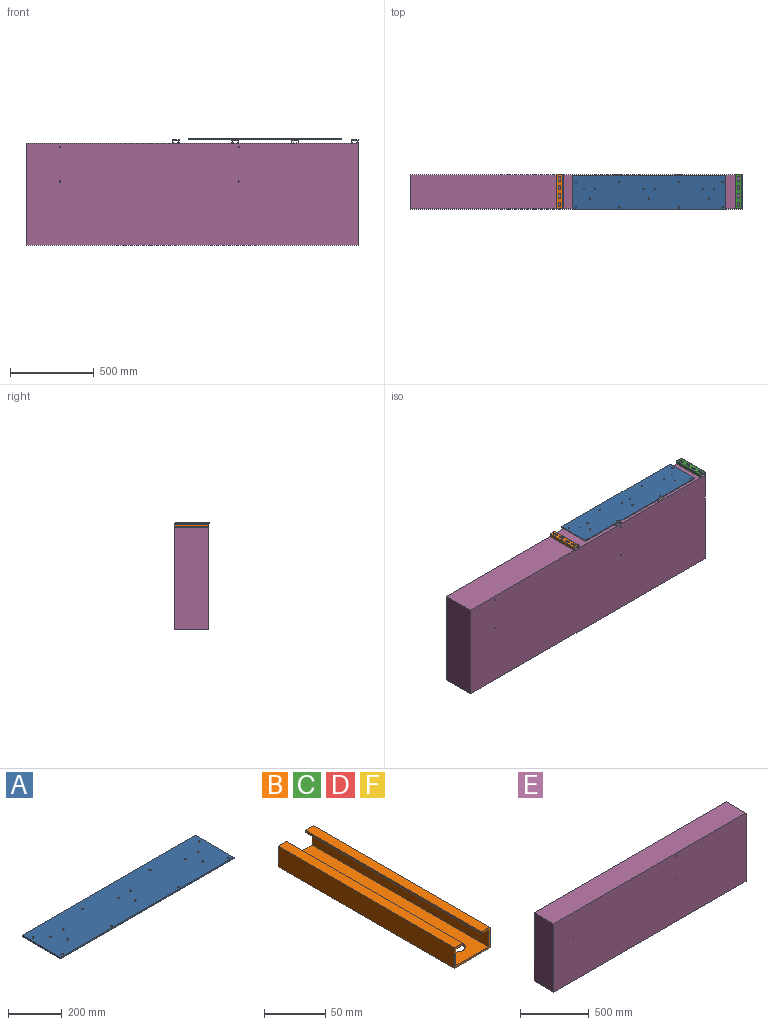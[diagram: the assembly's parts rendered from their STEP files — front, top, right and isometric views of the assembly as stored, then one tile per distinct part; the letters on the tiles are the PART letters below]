
ASSEMBLY  parts=6 mates=5
PART A: 23 faces, bbox 914.4x203.2x6.4 mm
  f0: plane 203.2x6.35mm, normal (1,0,0), area 1290.3mm2, adj f1,f3,f4,f5
  f1: plane 914.4x6.35mm, normal (0,1,0), area 5806.4mm2, adj f0,f2,f4,f5
  f2: plane 203.2x6.35mm, normal (-1,0,0), area 1290.3mm2, adj f1,f3,f4,f5
  f3: plane 914.4x6.35mm, normal (0,-1,0), area 5806.4mm2, adj f0,f2,f4,f5
  f4: plane 914.4x203.2mm, normal (0,0,1), area 184963.4mm2, adj f0,f1,f2,f3,f6,f7,f8,f9
  f5: plane 914.4x203.2mm, normal (0,0,-1), area 184963.4mm2, adj f0,f1,f2,f3,f6,f7,f8,f9
  f6: cylinder r=3.97mm len=7.94mm, axis (0,0,1), area 158.3mm2, adj f4,f5
  f7: cylinder r=3.97mm len=7.94mm, axis (0,0,1), area 158.3mm2, adj f4,f5
  f8: cylinder r=3.97mm len=7.94mm, axis (0,0,1), area 158.3mm2, adj f4,f5
  f9: cylinder r=3.97mm len=7.94mm, axis (0,0,1), area 158.3mm2, adj f4,f5
  f10: cylinder r=3.98mm len=7.95mm, axis (0,0,1), area 158.6mm2, adj f4,f5
  f11: cylinder r=3.98mm len=7.95mm, axis (0,0,1), area 158.6mm2, adj f4,f5
  f12: cylinder r=3.98mm len=7.95mm, axis (0,0,1), area 158.6mm2, adj f4,f5
  f13: cylinder r=3.98mm len=7.95mm, axis (0,0,1), area 158.6mm2, adj f4,f5
  f14: cylinder r=3.98mm len=7.95mm, axis (0,0,1), area 158.6mm2, adj f4,f5
  f15: cylinder r=3.98mm len=7.95mm, axis (0,0,1), area 158.6mm2, adj f4,f5
  f16: cylinder r=3.98mm len=7.95mm, axis (0,0,1), area 158.6mm2, adj f4,f5
  f17: cylinder r=3.98mm len=7.95mm, axis (0,0,1), area 158.6mm2, adj f4,f5
  f18: cylinder r=3.98mm len=7.95mm, axis (0,0,1), area 158.6mm2, adj f4,f5
  f19: cylinder r=3.97mm len=7.94mm, axis (0,0,1), area 158.3mm2, adj f4,f5
  f20: cylinder r=3.97mm len=7.94mm, axis (0,0,1), area 158.3mm2, adj f4,f5
  f21: cylinder r=3.97mm len=7.94mm, axis (0,0,1), area 158.3mm2, adj f4,f5
  f22: cylinder r=3.97mm len=7.94mm, axis (0,0,1), area 158.3mm2, adj f4,f5
PART B: 30 faces, bbox 41.3x203.2x20.6 mm
  f0: plane 203.2x9.53mm, normal (0,0,1), area 1935.5mm2, adj f1,f11,f12,f13
  f1: plane 203.2x20.64mm, normal (-1,0,0), area 4193.5mm2, adj f0,f2,f12,f13
  f2: plane 203.2x41.28mm, normal (0,0,-1), area 6927.7mm2, adj f1,f3,f12,f13,f14,f15,f16,f17
  f3: plane 203.2x20.64mm, normal (1,0,0), area 4193.5mm2, adj f2,f4,f12,f13
  f4: plane 203.2x9.53mm, normal (0,0,1), area 1935.5mm2, adj f3,f5,f12,f13
  f5: plane 203.2x2.03mm, normal (-1,0,0), area 412.9mm2, adj f4,f6,f12,f13
  f6: plane 203.2x7.49mm, normal (0,0,-1), area 1522.6mm2, adj f5,f7,f12,f13
  f7: plane 203.2x16.57mm, normal (-1,0,0), area 3367.7mm2, adj f6,f8,f12,f13
  f8: plane 203.2x37.21mm, normal (0,0,1), area 6101.9mm2, adj f7,f9,f12,f13,f14,f15,f16,f17
  f9: plane 203.2x16.57mm, normal (1,0,0), area 3367.7mm2, adj f8,f10,f12,f13
  f10: plane 203.2x7.49mm, normal (0,0,-1), area 1522.6mm2, adj f9,f11,f12,f13
  f11: plane 203.2x2.03mm, normal (1,0,0), area 412.9mm2, adj f0,f10,f12,f13
  f12: plane 41.28x20.64mm, normal (0,-1,0), area 189.9mm2, adj f0,f1,f2,f3,f4,f5,f6,f7
  f13: plane 41.28x20.64mm, normal (0,1,0), area 189.9mm2, adj f0,f1,f2,f3,f4,f5,f6,f7
  f14: cylinder r=7.11mm len=14.22mm, axis (0,0,-1), area 45.4mm2, adj f2,f8,f15,f17
  f15: plane 14.48x2.03mm, normal (1,0,0), area 29.4mm2, adj f2,f8,f14,f16
  f16: cylinder r=7.11mm len=14.22mm, axis (0,0,-1), area 45.4mm2, adj f2,f8,f15,f17
  f17: plane 14.48x2.03mm, normal (-1,0,0), area 29.4mm2, adj f2,f8,f14,f16
  f18: cylinder r=7.11mm len=14.22mm, axis (0,0,-1), area 45.4mm2, adj f2,f8,f19,f21
  f19: plane 14.48x2.03mm, normal (1,0,0), area 29.4mm2, adj f2,f8,f18,f20
  f20: cylinder r=7.11mm len=14.22mm, axis (0,0,-1), area 45.4mm2, adj f2,f8,f19,f21
  f21: plane 14.48x2.03mm, normal (-1,0,0), area 29.4mm2, adj f2,f8,f18,f20
  f22: cylinder r=7.11mm len=14.22mm, axis (0,0,-1), area 45.4mm2, adj f2,f8,f23,f25
  f23: plane 14.48x2.03mm, normal (1,0,0), area 29.4mm2, adj f2,f8,f22,f24
  f24: cylinder r=7.11mm len=14.22mm, axis (0,0,-1), area 45.4mm2, adj f2,f8,f23,f25
  f25: plane 14.48x2.03mm, normal (-1,0,0), area 29.4mm2, adj f2,f8,f22,f24
  f26: cylinder r=7.11mm len=14.22mm, axis (0,0,-1), area 45.4mm2, adj f2,f8,f27,f29
  f27: plane 14.48x2.03mm, normal (1,0,0), area 29.4mm2, adj f2,f8,f26,f28
  f28: cylinder r=7.11mm len=14.22mm, axis (0,0,-1), area 45.4mm2, adj f2,f8,f27,f29
  f29: plane 14.48x2.03mm, normal (-1,0,0), area 29.4mm2, adj f2,f8,f26,f28
PART C: same geometry as B
PART D: same geometry as B
PART E: 14 faces, bbox 1981.2x203.2x609.6 mm
  f0: plane 609.6x203.2mm, normal (1,0,0), area 123870.7mm2, adj f1,f3,f4,f5
  f1: plane 1981.2x203.2mm, normal (0,0,1), area 402579.8mm2, adj f0,f2,f4,f5
  f2: plane 609.6x203.2mm, normal (-1,0,0), area 123870.7mm2, adj f1,f3,f4,f5
  f3: plane 1981.2x203.2mm, normal (0,0,-1), area 402579.8mm2, adj f0,f2,f4,f5
  f4: plane 1981.2x609.6mm, normal (0,-1,0), area 1207612.8mm2, adj f0,f1,f2,f3,f6,f8,f10,f12
  f5: plane 1981.2x609.6mm, normal (0,1,0), area 1207739.5mm2, adj f0,f1,f2,f3
  f6: cylinder r=3.17mm len=50.8mm, axis (0,-1,0), area 1013.4mm2, adj f4,f7
  f7: plane 6.35x6.35mm, normal (0,-1,0), area 31.7mm2, adj f6
  f8: cylinder r=3.17mm len=50.8mm, axis (0,-1,0), area 1013.4mm2, adj f4,f9
  f9: plane 6.35x6.35mm, normal (0,-1,0), area 31.7mm2, adj f8
  f10: cylinder r=3.17mm len=50.8mm, axis (0,-1,0), area 1013.4mm2, adj f4,f11
  f11: plane 6.35x6.35mm, normal (0,-1,0), area 31.7mm2, adj f10
  f12: cylinder r=3.17mm len=50.8mm, axis (0,-1,0), area 1013.4mm2, adj f4,f13
  f13: plane 6.35x6.35mm, normal (0,-1,0), area 31.7mm2, adj f12
PART F: same geometry as B
PLACE A t=(-113.1,-295.22,362.25)mm
PLACE B rot(axis=(0,1,0),180deg) t=(-646.5,-191.2,362.25)mm
PLACE C rot(axis=(0,1,0),180deg) t=(420.3,-191.2,362.25)mm
PLACE D rot(axis=(0,1,0),180deg) t=(-290.9,-191.2,362.25)mm
PLACE E t=(-549.66,-191.2,36.82)mm fixed
PLACE F rot(axis=(0,1,0),180deg) t=(64.7,-191.2,362.25)mm
MATE planar C.f13 <-> E.f5  axis (0,1,0) through (440.94,-191.2,351.93)mm
MATE parallel E.f5 <-> A.f1  axis (0,1,0) through (-549.66,-191.2,36.82)mm
MATE planar E.f1 <-> C.f0  axis (0,0,1) through (-549.66,-292.8,341.62)mm
MATE planar C.f1 <-> E.f0  axis (1,0,0) through (440.94,-292.8,351.93)mm
MATE planar C.f22 <-> A.f5  axis (0,0,1) through (420.3,-274.58,362.25)mm
